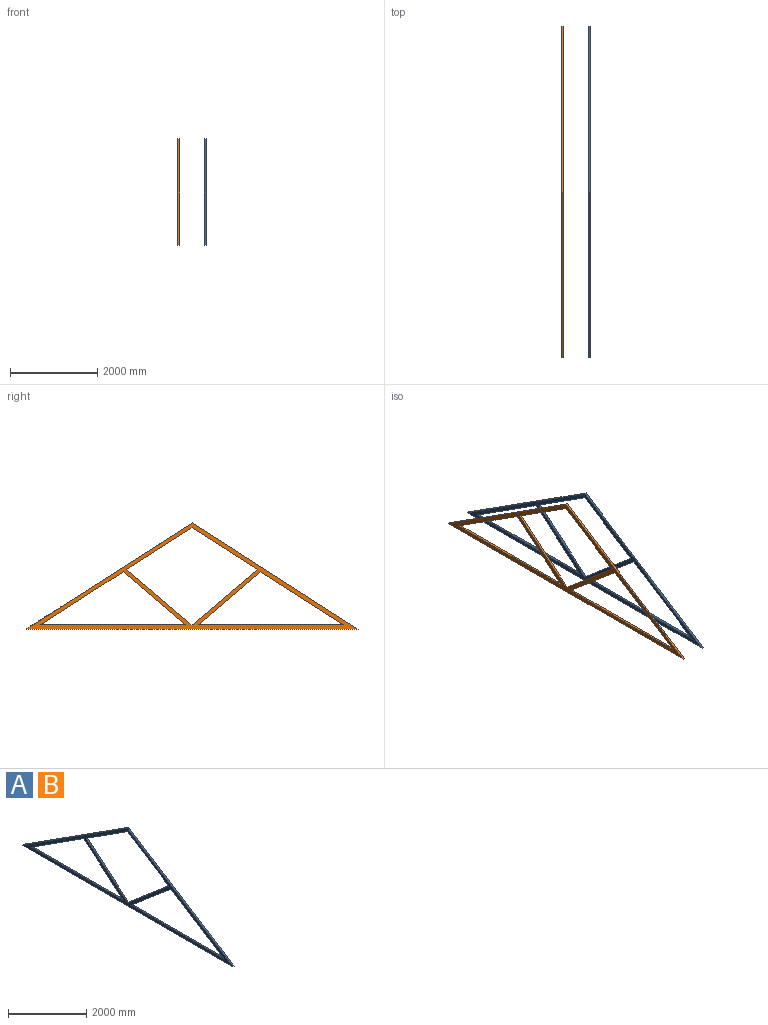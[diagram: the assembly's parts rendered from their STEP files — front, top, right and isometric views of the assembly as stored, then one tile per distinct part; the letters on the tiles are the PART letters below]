
ASSEMBLY  parts=2 mates=1
PART A: 15 faces, bbox 44.5x7620x2438.4 mm
  f0: plane 3810x2438.4mm, normal (0,0.54,0.84), area 201068.8mm2, adj f1,f12,f13,f14
  f1: plane 3810x2438.4mm, normal (0,-0.54,0.84), area 201068.8mm2, adj f0,f12,f13,f14
  f2: plane 1432.51x1219.2mm, normal (0,-0.65,-0.76), area 83614.9mm2, adj f3,f9,f13,f14
  f3: plane 3337.51x44.45mm, normal (0,0,1), area 148352.4mm2, adj f2,f9,f13,f14
  f4: plane 3337.51x44.45mm, normal (0,0,1), area 148352.4mm2, adj f5,f10,f13,f14
  f5: plane 1432.51x1219.2mm, normal (0,0.65,-0.76), area 83614.9mm2, adj f4,f10,f13,f14
  f6: plane 1495.59x957.18mm, normal (0,-0.54,-0.84), area 78928.2mm2, adj f7,f11,f13,f14
  f7: plane 1495.59x1272.89mm, normal (0,-0.65,0.76), area 87296.8mm2, adj f6,f8,f13,f14
  f8: plane 1495.59x1272.89mm, normal (0,0.65,0.76), area 87296.8mm2, adj f7,f11,f13,f14
  f9: plane 1905x1219.2mm, normal (0,0.54,-0.84), area 100534.4mm2, adj f2,f3,f13,f14
  f10: plane 1905x1219.2mm, normal (0,-0.54,-0.84), area 100534.4mm2, adj f4,f5,f13,f14
  f11: plane 1495.59x957.18mm, normal (0,0.54,-0.84), area 78928.2mm2, adj f6,f8,f13,f14
  f12: plane 7620x44.45mm, normal (0,0,-1), area 338709mm2, adj f0,f1,f13,f14
  f13: plane 7620x2438.4mm, normal (1,0,0), area 1885948.5mm2, adj f0,f1,f2,f3,f4,f5,f6,f7
  f14: plane 7620x2438.4mm, normal (-1,0,0), area 1885948.5mm2, adj f0,f1,f2,f3,f4,f5,f6,f7
PART B: same geometry as A
PLACE A t=(304.8,0,0)mm
PLACE B t=(-304.8,0,0)mm
MATE parallel A.f12 <-> B.f12  axis (0,0,-1) through (304.8,0,0)mm
